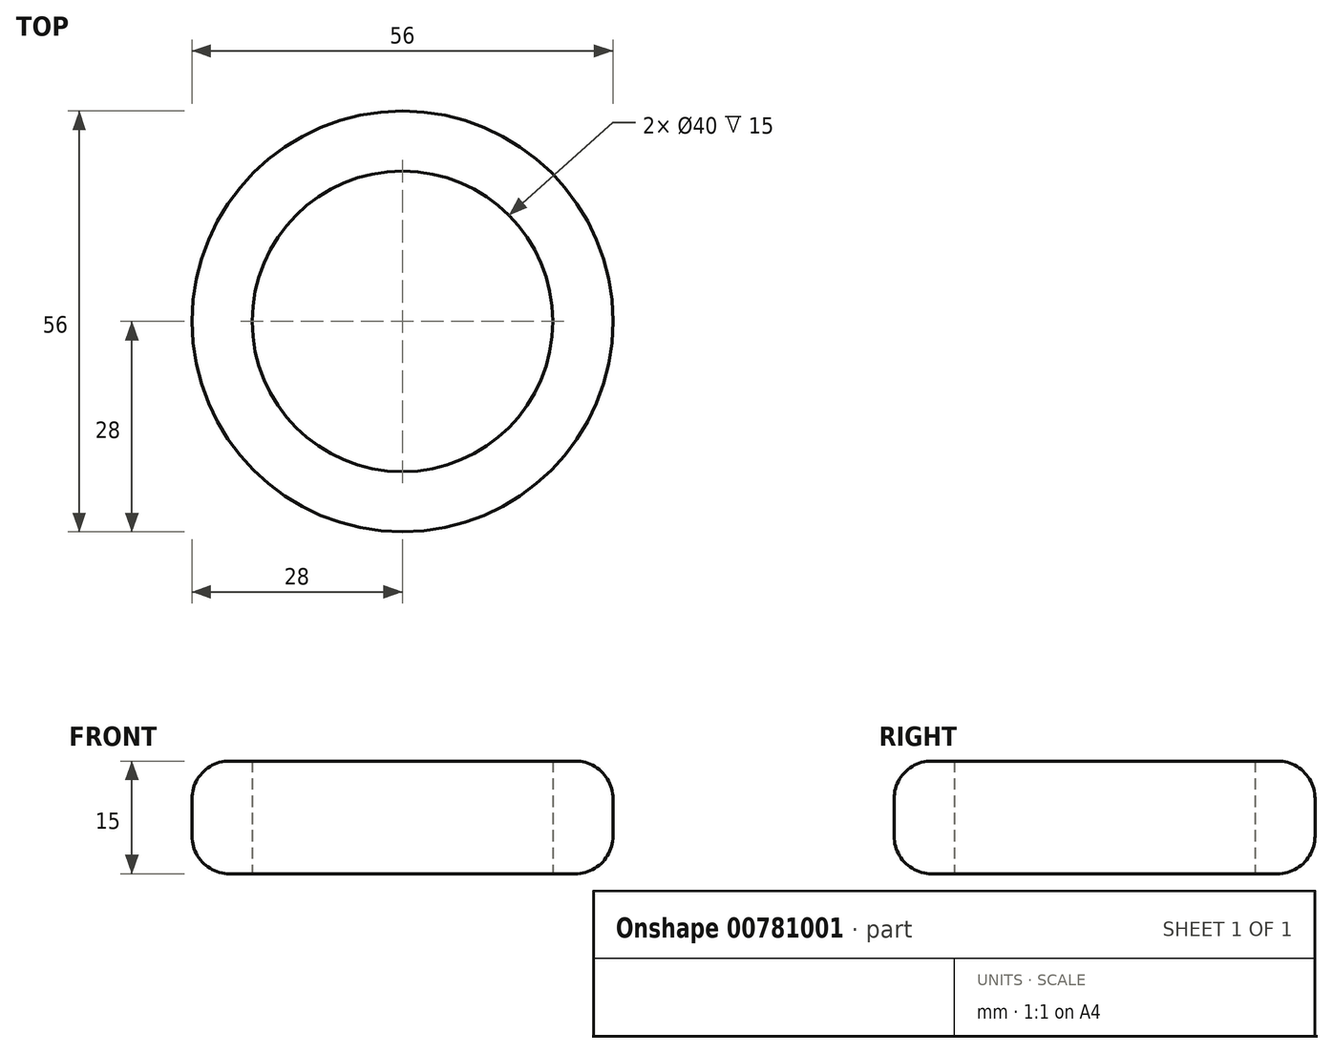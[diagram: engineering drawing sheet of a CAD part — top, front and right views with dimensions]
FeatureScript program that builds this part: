
annotation { "Feature Type Name" : "Feature", "Feature Type Description" : "" }
export const myFeature = defineFeature(function(context is Context, id is Id, definition is map)
    precondition{}
    {
        {
            var Q0;
            Q0=qCreatedBy(makeId("Top.planeOp"),FACE);
            var sketch = newSketch(context, id + "F0", { "sketchPlane" : qUnion([Q0])});
            skCircle(sketch, "E0", {"center": v(0, 0) * mm, "radius": 20 * mm});
            skCircle(sketch, "E1.0", {"center": v(0, 0) * mm, "radius": 28 * mm});
            skSolve(sketch);
        }
        {
            var Q0;
            Q0=makeQuery(id+"F0.imprint","IMPRINT",FACE,{"disambiguationData":[TD([[makeQuery(id+"F0.imprint","IMPRINT",EDGE,{"derivedFrom":sQuery(id+"F0.wireOp",EDGE,"E0")}),-1.0]])]});
            extrude(context, id + "F1", {"entities" : qUnion([Q0]), "endBound" : BoundingType.SYMMETRIC, "depth" : 15 * mm, "offsetDistance" : 25 * mm});
        }
        {
            var Q0;
            Q0=makeQuery(id+"F1.opExtrude","CAP_EDGE",EDGE,{"disambiguationData":[OSD([sQuery(id+"F0.wireOp",EDGE,"E1.0")])],"isStart":false});
            var Q1;
            Q1=makeQuery(id+"F1.opExtrude","CAP_EDGE",EDGE,{"disambiguationData":[OSD([sQuery(id+"F0.wireOp",EDGE,"E1.0")])],"isStart":true});
            fillet(context, id + "F2", {"entities" : qUnion([Q0, Q1]), "radius" : 5 * mm, "tangentPropagation" : true, "allowEdgeOverflow" : false});
        }
    });
